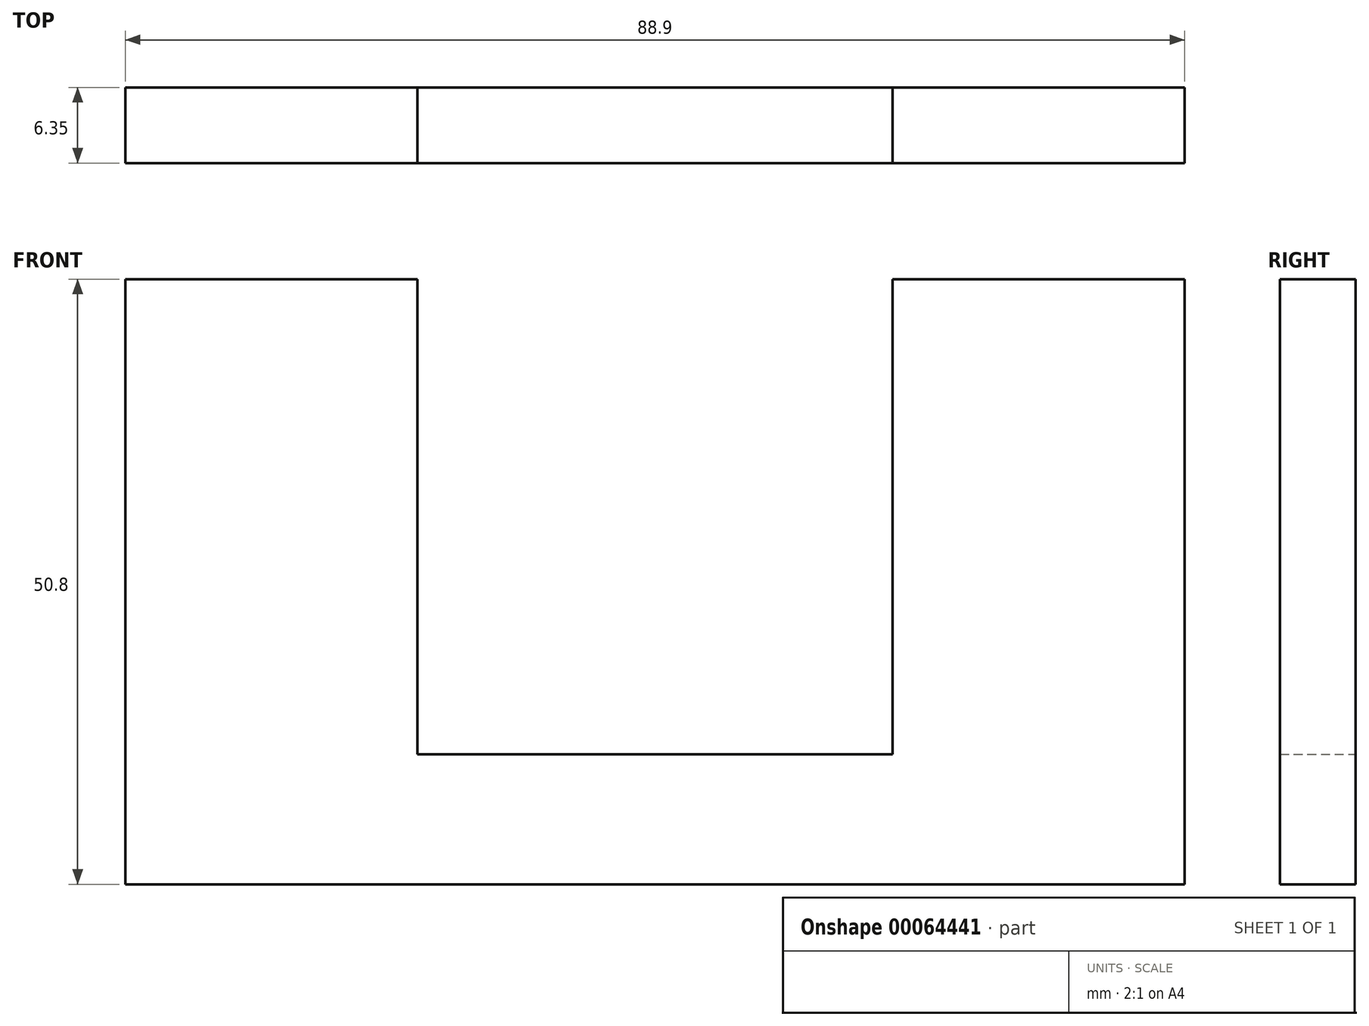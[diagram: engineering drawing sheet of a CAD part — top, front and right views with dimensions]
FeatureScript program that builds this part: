
annotation { "Feature Type Name" : "Feature", "Feature Type Description" : "" }
export const myFeature = defineFeature(function(context is Context, id is Id, definition is map)
    precondition{}
    {
        {
            var Q0;
            Q0=qCreatedBy(makeId("Front.planeOp"),FACE);
            var sketch = newSketch(context, id + "F0", { "sketchPlane" : qUnion([Q0])});
            skLineSegment(sketch, "E0.bottom", {"start": v(44.45, 25.4) * mm, "end": v(19.94, 25.4) * mm});
            skLineSegment(sketch, "E0.top", {"start": v(44.45, -25.4) * mm, "end": v(-44.45, -25.4) * mm});
            skLineSegment(sketch, "E0.left", {"start": v(44.45, 25.4) * mm, "end": v(44.45, -25.4) * mm});
            skLineSegment(sketch, "E0.right", {"start": v(-44.45, 25.4) * mm, "end": v(-44.45, -25.4) * mm});
            skPoint(sketch, "E0.middle", {"position": v(0, 0) * mm});
            skLineSegment(sketch, "E1.top", {"start": v(19.94, -14.48) * mm, "end": v(-19.94, -14.48) * mm});
            skLineSegment(sketch, "E1.left", {"start": v(19.94, 25.4) * mm, "end": v(19.94, -14.48) * mm});
            skLineSegment(sketch, "E1.right", {"start": v(-19.94, 25.4) * mm, "end": v(-19.94, -14.48) * mm});
            skPoint(sketch, "E1.middle", {"position": v(0, 5.46) * mm});
            skLineSegment(sketch, "E2.trimOffspring", {"start": v(-19.94, 25.4) * mm, "end": v(-44.45, 25.4) * mm});
            skSolve(sketch);
        }
        {
            var Q0;
            Q0 = qSketchRegion(id + "F0", true);
            extrude(context, id + "F1", {"entities" : qUnion([Q0]), "depth" : 6.35 * mm});
        }
        {
            var Q0;
            Q0 = qSketchRegion(id + "F0", true);
            extrude(context, id + "F2", {"entities" : qUnion([Q0]), "operationType" : NewBodyOperationType.ADD, "depth" : 6.35 * mm});
        }
    });
